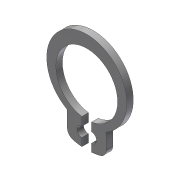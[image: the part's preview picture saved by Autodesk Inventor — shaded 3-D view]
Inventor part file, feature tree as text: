
AUTODESK INVENTOR PART (.ipt)
format: ipt  version: 2016 (Build 200138000, 138)  size: 93,696 bytes
history: native  units: in
note: dims shown in document units (in); Inventor stores cm internally (conversion verified against a paired STEP export)
features: other x1, fillet x1
ambient origin geometry x8: Origin, YZ Plane, XZ Plane, XY Plane, X Axis, Y Axis, Z Axis, Center Point
bodies: Solid1 (feature_tree)
feature tree (2):
  other  "circlips_din471_8_0_8"
  fillet  "Fillet1"  Radius=0.0394in
